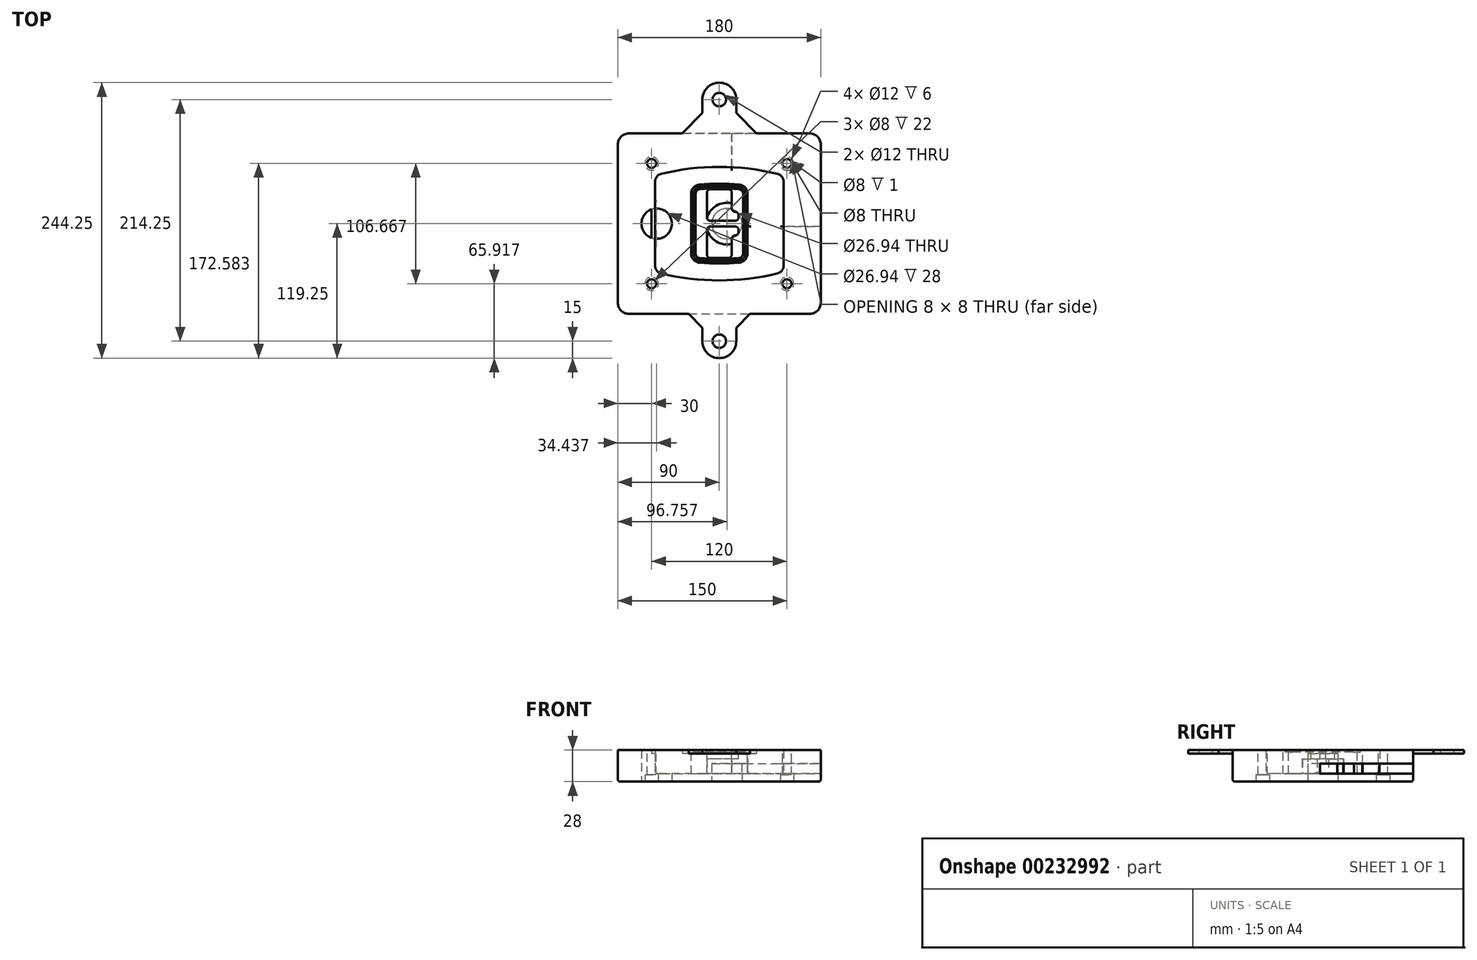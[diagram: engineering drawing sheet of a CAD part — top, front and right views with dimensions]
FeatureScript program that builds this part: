
annotation { "Feature Type Name" : "Feature", "Feature Type Description" : "" }
export const myFeature = defineFeature(function(context is Context, id is Id, definition is map)
    precondition{}
    {
        {
            var Q0;
            Q0=qCreatedBy(makeId("Top.planeOp"),FACE);
            var sketch = newSketch(context, id + "F0", { "sketchPlane" : qUnion([Q0])});
            skPoint(sketch, "E0.rect.middle", {"position": v(0, 0) * mm});
            skLineSegment(sketch, "E1.bottom", {"start": v(-80, -80) * mm, "end": v(80, -80) * mm});
            skLineSegment(sketch, "E1.top", {"start": v(-80, 80) * mm, "end": v(80, 80) * mm});
            skLineSegment(sketch, "E1.left", {"start": v(-90, -70) * mm, "end": v(-90, 70) * mm});
            skLineSegment(sketch, "E1.right", {"start": v(90, -70) * mm, "end": v(90, 70) * mm});
            skLineSegment(sketch, "E2", {"start": v(-90, 80) * mm, "end": v(90, -80) * mm, "construction": true});
            skLineSegment(sketch, "E3", {"start": v(90, 80) * mm, "end": v(-90, -80) * mm, "construction": true});
            skCircle(sketch, "E4", {"center": v(-60, 53.33) * mm, "radius": 4 * mm});
            skCircle(sketch, "E5", {"center": v(60, 53.33) * mm, "radius": 4 * mm});
            skCircle(sketch, "E6", {"center": v(60, -53.33) * mm, "radius": 4 * mm});
            skCircle(sketch, "E7", {"center": v(-60, -53.33) * mm, "radius": 4 * mm});
            skLineSegment(sketch, "E8", {"start": v(-60, 53.33) * mm, "end": v(60, 53.33) * mm, "construction": true});
            skLineSegment(sketch, "E9", {"start": v(60, 53.33) * mm, "end": v(60, -53.33) * mm, "construction": true});
            skLineSegment(sketch, "E10", {"start": v(60, -53.33) * mm, "end": v(-60, -53.33) * mm, "construction": true});
            skLineSegment(sketch, "E11", {"start": v(-60, -53.33) * mm, "end": v(-60, 53.33) * mm, "construction": true});
            skLineSegment(sketch, "E12", {"start": v(-60, 37.3) * mm, "end": v(-60, -37.3) * mm});
            skLineSegment(sketch, "E13", {"start": v(60, 37.3) * mm, "end": v(60, -37.3) * mm});
            skArc(sketch, "E14", {"start": v(52.38, 47.01) * mm, "mid": v(0, 53.33) * mm, "end": v(-52.38, 47.01) * mm});
            skArc(sketch, "E15", {"start": v(-52.38, -47.01) * mm, "mid": v(0, -53.33) * mm, "end": v(52.38, -47.01) * mm});
            skLineSegment(sketch, "E16", {"start": v(-60, 0) * mm, "end": v(60, 0) * mm, "construction": true});
            skPoint(sketch, "E17.visualSharp", {"position": v(-60, -45) * mm});
            skArc(sketch, "E17.filletArc", {"start": v(-60, -37.3) * mm, "mid": v(-57.87, -43.47) * mm, "end": v(-52.38, -47.01) * mm});
            skPoint(sketch, "E18.visualSharp", {"position": v(-60, 45) * mm});
            skArc(sketch, "E18.filletArc", {"start": v(-52.38, 47.01) * mm, "mid": v(-57.87, 43.47) * mm, "end": v(-60, 37.3) * mm});
            skPoint(sketch, "E19.visualSharp", {"position": v(60, 45) * mm});
            skArc(sketch, "E19.filletArc", {"start": v(60, 37.3) * mm, "mid": v(57.87, 43.47) * mm, "end": v(52.38, 47.01) * mm});
            skPoint(sketch, "E20.visualSharp", {"position": v(60, -45) * mm});
            skArc(sketch, "E20.filletArc", {"start": v(52.38, -47.01) * mm, "mid": v(57.87, -43.47) * mm, "end": v(60, -37.3) * mm});
            skPoint(sketch, "E21.visualSharp", {"position": v(-90, 80) * mm});
            skArc(sketch, "E21.filletArc", {"start": v(-80, 80) * mm, "mid": v(-87.07, 77.07) * mm, "end": v(-90, 70) * mm});
            skPoint(sketch, "E22.visualSharp", {"position": v(90, 80) * mm});
            skArc(sketch, "E22.filletArc", {"start": v(90, 70) * mm, "mid": v(87.07, 77.07) * mm, "end": v(80, 80) * mm});
            skPoint(sketch, "E23.visualSharp", {"position": v(90, -80) * mm});
            skArc(sketch, "E23.filletArc", {"start": v(80, -80) * mm, "mid": v(87.07, -77.07) * mm, "end": v(90, -70) * mm});
            skPoint(sketch, "E24.visualSharp", {"position": v(-90, -80) * mm});
            skArc(sketch, "E24.filletArc", {"start": v(-90, -70) * mm, "mid": v(-87.07, -77.07) * mm, "end": v(-80, -80) * mm});
            skArc(sketch, "E25.0", {"start": v(57, 37.3) * mm, "mid": v(55.5, 41.62) * mm, "end": v(51.67, 44.1) * mm});
            skLineSegment(sketch, "E25.1", {"start": v(57, 37.3) * mm, "end": v(57, -37.3) * mm});
            skArc(sketch, "E25.2", {"start": v(51.67, -44.1) * mm, "mid": v(55.5, -41.62) * mm, "end": v(57, -37.3) * mm});
            skArc(sketch, "E25.3", {"start": v(-51.67, -44.1) * mm, "mid": v(0, -50.33) * mm, "end": v(51.67, -44.1) * mm});
            skArc(sketch, "E25.4", {"start": v(-57, -37.3) * mm, "mid": v(-55.5, -41.62) * mm, "end": v(-51.67, -44.1) * mm});
            skArc(sketch, "E25.5", {"start": v(51.67, 44.1) * mm, "mid": v(0, 50.33) * mm, "end": v(-51.67, 44.1) * mm});
            skLineSegment(sketch, "E25.6", {"start": v(-57, 37.3) * mm, "end": v(-57, -37.3) * mm});
            skArc(sketch, "E25.7", {"start": v(-51.67, 44.1) * mm, "mid": v(-55.5, 41.62) * mm, "end": v(-57, 37.3) * mm});
            skArc(sketch, "E26.0", {"start": v(-53.33, 50.9) * mm, "mid": v(-61.01, 45.94) * mm, "end": v(-64, 37.3) * mm});
            skArc(sketch, "E26.1", {"start": v(53.33, 50.9) * mm, "mid": v(0, 57.33) * mm, "end": v(-53.33, 50.9) * mm});
            skArc(sketch, "E26.2", {"start": v(64, 37.3) * mm, "mid": v(61.01, 45.94) * mm, "end": v(53.33, 50.9) * mm});
            skLineSegment(sketch, "E26.3", {"start": v(64, 37.3) * mm, "end": v(64, -37.3) * mm});
            skArc(sketch, "E26.4", {"start": v(53.33, -50.9) * mm, "mid": v(61.01, -45.94) * mm, "end": v(64, -37.3) * mm});
            skLineSegment(sketch, "E26.5", {"start": v(-64, 37.3) * mm, "end": v(-64, -37.3) * mm});
            skArc(sketch, "E26.6", {"start": v(-53.33, -50.9) * mm, "mid": v(0, -57.33) * mm, "end": v(53.33, -50.9) * mm});
            skArc(sketch, "E26.7", {"start": v(-64, -37.3) * mm, "mid": v(-61.01, -45.94) * mm, "end": v(-53.33, -50.9) * mm});
            skSolve(sketch);
        }
        {
            var Q0;
            Q0=makeQuery(id+"F0.imprint","IMPRINT",FACE,{"disambiguationData":[TD([[makeQuery(id+"F0.imprint","IMPRINT",EDGE,{"derivedFrom":sQuery(id+"F0.wireOp",EDGE,"E1.bottom")}),1.0]])]});
            var Q1;
            Q1=makeQuery(id+"F0.imprint","IMPRINT",FACE,{"disambiguationData":[TD([[makeQuery(id+"F0.imprint","IMPRINT",EDGE,{"derivedFrom":sQuery(id+"F0.wireOp",EDGE,"E12")}),1.0]])]});
            var Q2;
            Q2=makeQuery(id+"F0.imprint","IMPRINT",FACE,{"disambiguationData":[TD([[makeQuery(id+"F0.imprint","IMPRINT",EDGE,{"derivedFrom":sQuery(id+"F0.wireOp",EDGE,"E25.0")}),1.0]])]});
            var Q3;
            Q3=makeQuery(id+"F0.imprint","IMPRINT",FACE,{"disambiguationData":[TD([[makeQuery(id+"F0.imprint","IMPRINT",EDGE,{"derivedFrom":sQuery(id+"F0.wireOp",EDGE,"E12")}),-1.0]])]});
            extrude(context, id + "F1", {"entities" : qUnion([Q0, Q1, Q2, Q3]), "oppositeDirection" : true, "depth" : 25 * mm});
        }
        {
            var Q0;
            Q0=makeQuery(id+"F0.imprint","IMPRINT",FACE,{"disambiguationData":[TD([[makeQuery(id+"F0.imprint","IMPRINT",EDGE,{"derivedFrom":sQuery(id+"F0.wireOp",EDGE,"E12")}),1.0]])]});
            extrude(context, id + "F2", {"entities" : qUnion([Q0]), "operationType" : NewBodyOperationType.ADD, "depth" : 3 * mm});
        }
        {
            var Q0;
            Q0=makeQuery(id+"F0.imprint","IMPRINT",FACE,{"disambiguationData":[TD([[makeQuery(id+"F0.imprint","IMPRINT",EDGE,{"derivedFrom":sQuery(id+"F0.wireOp",EDGE,"E25.0")}),1.0]])]});
            extrude(context, id + "F3", {"entities" : qUnion([Q0]), "operationType" : NewBodyOperationType.REMOVE, "oppositeDirection" : true, "depth" : 18 * mm});
        }
        {
            var Q0;
            Q0=makeQuery(id+"F2.opExtrude","CAP_FACE",FACE,{"disambiguationData":[OSD([sQuery(id+"F0.wireOp",EDGE,"E12"),sQuery(id+"F0.wireOp",EDGE,"E13"),sQuery(id+"F0.wireOp",EDGE,"E14"),sQuery(id+"F0.wireOp",EDGE,"E15"),sQuery(id+"F0.wireOp",EDGE,"E17.filletArc"),sQuery(id+"F0.wireOp",EDGE,"E18.filletArc"),sQuery(id+"F0.wireOp",EDGE,"E19.filletArc"),sQuery(id+"F0.wireOp",EDGE,"E20.filletArc"),sQuery(id+"F0.wireOp",EDGE,"E25.0"),sQuery(id+"F0.wireOp",EDGE,"E25.1"),sQuery(id+"F0.wireOp",EDGE,"E25.2"),sQuery(id+"F0.wireOp",EDGE,"E25.3"),sQuery(id+"F0.wireOp",EDGE,"E25.4"),sQuery(id+"F0.wireOp",EDGE,"E25.5"),sQuery(id+"F0.wireOp",EDGE,"E25.6"),sQuery(id+"F0.wireOp",EDGE,"E25.7")])],"isStart":false});
            var sketch = newSketch(context, id + "F4", { "sketchPlane" : qUnion([Q0])});
            skArc(sketch, "E27.0", {"start": v(-17.7, -34.56) * mm, "mid": v(0, -35.33) * mm, "end": v(17.7, -34.56) * mm});
            skArc(sketch, "E28.0", {"start": v(17.7, 34.56) * mm, "mid": v(0, 35.33) * mm, "end": v(-17.7, 34.56) * mm});
            skLineSegment(sketch, "E29", {"start": v(-25, 26.59) * mm, "end": v(-25, -26.59) * mm});
            skLineSegment(sketch, "E30", {"start": v(25, 26.59) * mm, "end": v(25, -26.59) * mm});
            skLineSegment(sketch, "E31", {"start": v(-25, 33.78) * mm, "end": v(25, 33.78) * mm, "construction": true});
            skLineSegment(sketch, "E32", {"start": v(-25, -33.78) * mm, "end": v(25, -33.78) * mm, "construction": true});
            skPoint(sketch, "E33.visualSharp", {"position": v(-25, 33.78) * mm});
            skArc(sketch, "E33.filletArc", {"start": v(-17.7, 34.56) * mm, "mid": v(-22.9, 32) * mm, "end": v(-25, 26.59) * mm});
            skPoint(sketch, "E34.visualSharp", {"position": v(25, 33.78) * mm});
            skArc(sketch, "E34.filletArc", {"start": v(25, 26.59) * mm, "mid": v(22.9, 32) * mm, "end": v(17.7, 34.56) * mm});
            skPoint(sketch, "E35.visualSharp", {"position": v(25, -33.78) * mm});
            skArc(sketch, "E35.filletArc", {"start": v(17.7, -34.56) * mm, "mid": v(22.9, -32) * mm, "end": v(25, -26.59) * mm});
            skPoint(sketch, "E36.visualSharp", {"position": v(-25, -33.78) * mm});
            skArc(sketch, "E36.filletArc", {"start": v(-25, -26.59) * mm, "mid": v(-22.9, -32) * mm, "end": v(-17.7, -34.56) * mm});
            skArc(sketch, "E37.0", {"start": v(51.67, 44.1) * mm, "mid": v(0, 50.33) * mm, "end": v(-51.67, 44.1) * mm});
            skArc(sketch, "E37.1", {"start": v(-51.67, 44.1) * mm, "mid": v(-55.5, 41.62) * mm, "end": v(-57, 37.3) * mm});
            skLineSegment(sketch, "E37.2", {"start": v(-57, 37.3) * mm, "end": v(-57, -37.3) * mm});
            skArc(sketch, "E37.3", {"start": v(-57, -37.3) * mm, "mid": v(-55.5, -41.62) * mm, "end": v(-51.67, -44.1) * mm});
            skArc(sketch, "E37.4", {"start": v(-51.67, -44.1) * mm, "mid": v(0, -50.33) * mm, "end": v(51.67, -44.1) * mm});
            skArc(sketch, "E37.5", {"start": v(51.67, -44.1) * mm, "mid": v(55.5, -41.62) * mm, "end": v(57, -37.3) * mm});
            skLineSegment(sketch, "E37.6", {"start": v(57, 37.3) * mm, "end": v(57, -37.3) * mm});
            skArc(sketch, "E37.7", {"start": v(57, 37.3) * mm, "mid": v(55.5, 41.62) * mm, "end": v(51.67, 44.1) * mm});
            skLineSegment(sketch, "E38.0", {"start": v(23, 26.59) * mm, "end": v(23, -26.59) * mm});
            skArc(sketch, "E38.1", {"start": v(17.53, -32.56) * mm, "mid": v(21.42, -30.64) * mm, "end": v(23, -26.59) * mm});
            skArc(sketch, "E38.2", {"start": v(-17.53, -32.56) * mm, "mid": v(0, -33.33) * mm, "end": v(17.53, -32.56) * mm});
            skArc(sketch, "E38.3", {"start": v(-23, -26.59) * mm, "mid": v(-21.42, -30.64) * mm, "end": v(-17.53, -32.56) * mm});
            skLineSegment(sketch, "E38.4", {"start": v(-23, 26.59) * mm, "end": v(-23, -26.59) * mm});
            skArc(sketch, "E38.5", {"start": v(23, 26.59) * mm, "mid": v(21.42, 30.64) * mm, "end": v(17.53, 32.56) * mm});
            skArc(sketch, "E38.6", {"start": v(-17.53, 32.56) * mm, "mid": v(-21.42, 30.64) * mm, "end": v(-23, 26.59) * mm});
            skArc(sketch, "E38.7", {"start": v(17.53, 32.56) * mm, "mid": v(0, 33.33) * mm, "end": v(-17.53, 32.56) * mm});
            skArc(sketch, "E39.0", {"start": v(21, 26.59) * mm, "mid": v(19.95, 29.29) * mm, "end": v(17.35, 30.57) * mm});
            skLineSegment(sketch, "E39.1", {"start": v(21, 26.59) * mm, "end": v(21, -26.59) * mm});
            skArc(sketch, "E39.2", {"start": v(17.35, -30.57) * mm, "mid": v(19.95, -29.29) * mm, "end": v(21, -26.59) * mm});
            skArc(sketch, "E39.3", {"start": v(-17.35, -30.57) * mm, "mid": v(0, -31.33) * mm, "end": v(17.35, -30.57) * mm});
            skArc(sketch, "E39.4", {"start": v(-21, -26.59) * mm, "mid": v(-19.95, -29.29) * mm, "end": v(-17.35, -30.57) * mm});
            skArc(sketch, "E39.5", {"start": v(17.35, 30.57) * mm, "mid": v(0, 31.33) * mm, "end": v(-17.35, 30.57) * mm});
            skLineSegment(sketch, "E39.6", {"start": v(-21, 26.59) * mm, "end": v(-21, -26.59) * mm});
            skArc(sketch, "E39.7", {"start": v(-17.35, 30.57) * mm, "mid": v(-19.95, 29.29) * mm, "end": v(-21, 26.59) * mm});
            skLineSegment(sketch, "E40", {"start": v(-25, 0) * mm, "end": v(25, 0) * mm, "construction": true});
            skLineSegment(sketch, "E41", {"start": v(-11, 5.5) * mm, "end": v(-11, 27.5) * mm});
            skLineSegment(sketch, "E42", {"start": v(-8, 30.5) * mm, "end": v(8, 30.5) * mm});
            skLineSegment(sketch, "E43", {"start": v(11, 27.5) * mm, "end": v(11, 13.5) * mm});
            skLineSegment(sketch, "E44", {"start": v(14, 10.5) * mm, "end": v(14, 10.5) * mm});
            skLineSegment(sketch, "E45", {"start": v(17, 7.5) * mm, "end": v(17, 5.5) * mm});
            skLineSegment(sketch, "E46", {"start": v(14, 2.5) * mm, "end": v(-8, 2.5) * mm});
            skPoint(sketch, "E47.visualSharp", {"position": v(-11, 30.5) * mm});
            skArc(sketch, "E47.filletArc", {"start": v(-8, 30.5) * mm, "mid": v(-10.12, 29.62) * mm, "end": v(-11, 27.5) * mm});
            skPoint(sketch, "E48.visualSharp", {"position": v(11, 30.5) * mm});
            skArc(sketch, "E48.filletArc", {"start": v(11, 27.5) * mm, "mid": v(10.12, 29.62) * mm, "end": v(8, 30.5) * mm});
            skPoint(sketch, "E49.visualSharp", {"position": v(11, 10.5) * mm});
            skArc(sketch, "E49.filletArc", {"start": v(11, 13.5) * mm, "mid": v(11.88, 11.38) * mm, "end": v(14, 10.5) * mm});
            skPoint(sketch, "E50.visualSharp", {"position": v(17, 10.5) * mm});
            skArc(sketch, "E50.filletArc", {"start": v(17, 7.5) * mm, "mid": v(16.12, 9.62) * mm, "end": v(14, 10.5) * mm});
            skPoint(sketch, "E51.visualSharp", {"position": v(17, 2.5) * mm});
            skArc(sketch, "E51.filletArc", {"start": v(14, 2.5) * mm, "mid": v(16.12, 3.38) * mm, "end": v(17, 5.5) * mm});
            skPoint(sketch, "E52.visualSharp", {"position": v(-11, 2.5) * mm});
            skArc(sketch, "E52.filletArc", {"start": v(-11, 5.5) * mm, "mid": v(-10.12, 3.38) * mm, "end": v(-8, 2.5) * mm});
            skLineSegment(sketch, "E53.0.MirrorCS", {"start": v(14, -2.5) * mm, "end": v(-8, -2.5) * mm});
            skArc(sketch, "E54.0.MirrorCS", {"start": v(-11, -5.5) * mm, "mid": v(-10.12, -3.38) * mm, "end": v(-8, -2.5) * mm});
            skLineSegment(sketch, "E55.0.MirrorCS", {"start": v(-11, -5.5) * mm, "end": v(-11, -27.5) * mm});
            skArc(sketch, "E56.0.MirrorCS", {"start": v(-8, -30.5) * mm, "mid": v(-10.12, -29.62) * mm, "end": v(-11, -27.5) * mm});
            skLineSegment(sketch, "E57.0.MirrorCS", {"start": v(-8, -30.5) * mm, "end": v(8, -30.5) * mm});
            skArc(sketch, "E58.0.MirrorCS", {"start": v(11, -27.5) * mm, "mid": v(10.12, -29.62) * mm, "end": v(8, -30.5) * mm});
            skLineSegment(sketch, "E59.0.MirrorCS", {"start": v(11, -27.5) * mm, "end": v(11, -13.5) * mm});
            skArc(sketch, "E60.0.MirrorCS", {"start": v(11, -13.5) * mm, "mid": v(11.88, -11.38) * mm, "end": v(14, -10.5) * mm});
            skArc(sketch, "E61.0.MirrorCS", {"start": v(17, -7.5) * mm, "mid": v(16.12, -9.62) * mm, "end": v(14, -10.5) * mm});
            skLineSegment(sketch, "E62.0.MirrorCS", {"start": v(17, -7.5) * mm, "end": v(17, -5.5) * mm});
            skArc(sketch, "E63.0.MirrorCS", {"start": v(14, -2.5) * mm, "mid": v(16.12, -3.38) * mm, "end": v(17, -5.5) * mm});
            skSolve(sketch);
        }
        {
            var Q0;
            Q0=makeQuery(id+"F4.imprint","IMPRINT",FACE,{"disambiguationData":[TD([[makeQuery(id+"F4.imprint","IMPRINT",EDGE,{"derivedFrom":sQuery(id+"F4.wireOp",EDGE,"E27.0")}),1.0]])]});
            var Q1;
            Q1=makeQuery(id+"F4.imprint","IMPRINT",FACE,{"disambiguationData":[TD([[makeQuery(id+"F4.imprint","IMPRINT",EDGE,{"derivedFrom":sQuery(id+"F4.wireOp",EDGE,"E38.0")}),-1.0]])]});
            var Q2;
            Q2=makeQuery(id+"F4.imprint","IMPRINT",FACE,{"disambiguationData":[TD([[makeQuery(id+"F4.imprint","IMPRINT",EDGE,{"derivedFrom":sQuery(id+"F4.wireOp",EDGE,"E39.0")}),1.0]])]});
            extrude(context, id + "F5", {"entities" : qUnion([Q0, Q1, Q2]), "operationType" : NewBodyOperationType.ADD, "endBound" : BoundingType.UP_TO_NEXT, "oppositeDirection" : true, "depth" : 25 * mm});
        }
        {
            var Q0;
            Q0=makeQuery(id+"F4.imprint","IMPRINT",FACE,{"disambiguationData":[TD([[makeQuery(id+"F4.imprint","IMPRINT",EDGE,{"derivedFrom":sQuery(id+"F4.wireOp",EDGE,"E38.0")}),-1.0]])]});
            extrude(context, id + "F6", {"entities" : qUnion([Q0]), "operationType" : NewBodyOperationType.REMOVE, "oppositeDirection" : true, "depth" : 2 * mm});
        }
        {
            var Q0;
            Q0=makeQuery(id+"F1.opExtrude","CAP_FACE",FACE,{"disambiguationData":[OSD([sQuery(id+"F0.wireOp",EDGE,"E1.bottom"),sQuery(id+"F0.wireOp",EDGE,"E1.top"),sQuery(id+"F0.wireOp",EDGE,"E1.left"),sQuery(id+"F0.wireOp",EDGE,"E1.right"),sQuery(id+"F0.wireOp",EDGE,"E4"),sQuery(id+"F0.wireOp",EDGE,"E5"),sQuery(id+"F0.wireOp",EDGE,"E6"),sQuery(id+"F0.wireOp",EDGE,"E7"),sQuery(id+"F0.wireOp",EDGE,"E21.filletArc"),sQuery(id+"F0.wireOp",EDGE,"E22.filletArc"),sQuery(id+"F0.wireOp",EDGE,"E23.filletArc"),sQuery(id+"F0.wireOp",EDGE,"E24.filletArc")])],"isStart":false});
            var sketch = newSketch(context, id + "F7", { "sketchPlane" : qUnion([Q0])});
            skCircle(sketch, "E64", {"center": v(6.76, 0) * mm, "radius": 13.47 * mm});
            skCircle(sketch, "E65", {"center": v(-55.56, 0) * mm, "radius": 13.47 * mm});
            skLineSegment(sketch, "E66", {"start": v(90, 0) * mm, "end": v(-90, 0) * mm});
            skCircle(sketch, "E67", {"center": v(6.76, 0) * mm, "radius": 18.47 * mm});
            skCircle(sketch, "E68", {"center": v(60, -53.33) * mm, "radius": 6 * mm});
            skCircle(sketch, "E69", {"center": v(-60, -53.33) * mm, "radius": 6 * mm});
            skCircle(sketch, "E70", {"center": v(-60, 53.33) * mm, "radius": 6 * mm});
            skCircle(sketch, "E71", {"center": v(60, 53.33) * mm, "radius": 6 * mm});
            skSolve(sketch);
        }
        {
            var Q0;
            {var subQ1=sQuery(id+"F7.wireOp",EDGE,"E66");var subQ4=sQuery(id+"F7.wireOp",EDGE,"E64");var subQ6=makeQuery(id+"F7.imprint","INTERSECT",VERTEX,{"disambiguationData":[OD(0.0)],"derivedFrom":[subQ4,subQ1]});Q0=makeQuery(id+"F7.imprint","IMPRINT",FACE,{"disambiguationData":[TD([[makeQuery(id+"F7.imprint","IMPRINT",EDGE,{"disambiguationData":[TD([[subQ6,-1.0]])],"derivedFrom":subQ4}),-1.0]])]});}
            var Q1;
            {var subQ0=sQuery(id+"F7.wireOp",EDGE,"E66");var subQ1=sQuery(id+"F7.wireOp",EDGE,"E64");var subQ3=makeQuery(id+"F7.imprint","INTERSECT",VERTEX,{"disambiguationData":[OD(0.0)],"derivedFrom":[subQ1,subQ0]});Q1=makeQuery(id+"F7.imprint","IMPRINT",FACE,{"disambiguationData":[TD([[makeQuery(id+"F7.imprint","IMPRINT",EDGE,{"disambiguationData":[TD([[subQ3,-1.0]])],"derivedFrom":subQ1}),1.0]])]});}
            var Q2;
            {var subQ0=sQuery(id+"F7.wireOp",EDGE,"E66");var subQ1=sQuery(id+"F7.wireOp",EDGE,"E64");var subQ3=makeQuery(id+"F7.imprint","INTERSECT",VERTEX,{"disambiguationData":[OD(0.0)],"derivedFrom":[subQ1,subQ0]});Q2=makeQuery(id+"F7.imprint","IMPRINT",FACE,{"disambiguationData":[TD([[makeQuery(id+"F7.imprint","IMPRINT",EDGE,{"disambiguationData":[TD([[subQ3,1.0]])],"derivedFrom":subQ1}),1.0]])]});}
            var Q3;
            {var subQ1=sQuery(id+"F7.wireOp",EDGE,"E66");var subQ4=sQuery(id+"F7.wireOp",EDGE,"E64");var subQ6=makeQuery(id+"F7.imprint","INTERSECT",VERTEX,{"disambiguationData":[OD(0.0)],"derivedFrom":[subQ4,subQ1]});Q3=makeQuery(id+"F7.imprint","IMPRINT",FACE,{"disambiguationData":[TD([[makeQuery(id+"F7.imprint","IMPRINT",EDGE,{"disambiguationData":[TD([[subQ6,1.0]])],"derivedFrom":subQ4}),-1.0]])]});}
            extrude(context, id + "F8", {"entities" : qUnion([Q0, Q1, Q2, Q3]), "operationType" : NewBodyOperationType.ADD, "oppositeDirection" : true, "depth" : 20 * mm});
        }
        {
            var Q0;
            {var subQ0=sQuery(id+"F7.wireOp",EDGE,"E66");var subQ1=sQuery(id+"F7.wireOp",EDGE,"E64");var subQ3=makeQuery(id+"F7.imprint","INTERSECT",VERTEX,{"disambiguationData":[OD(0.0)],"derivedFrom":[subQ1,subQ0]});Q0=makeQuery(id+"F7.imprint","IMPRINT",FACE,{"disambiguationData":[TD([[makeQuery(id+"F7.imprint","IMPRINT",EDGE,{"disambiguationData":[TD([[subQ3,-1.0]])],"derivedFrom":subQ1}),1.0]])]});}
            var Q1;
            {var subQ0=sQuery(id+"F7.wireOp",EDGE,"E66");var subQ1=sQuery(id+"F7.wireOp",EDGE,"E64");var subQ3=makeQuery(id+"F7.imprint","INTERSECT",VERTEX,{"disambiguationData":[OD(0.0)],"derivedFrom":[subQ1,subQ0]});Q1=makeQuery(id+"F7.imprint","IMPRINT",FACE,{"disambiguationData":[TD([[makeQuery(id+"F7.imprint","IMPRINT",EDGE,{"disambiguationData":[TD([[subQ3,1.0]])],"derivedFrom":subQ1}),1.0]])]});}
            extrude(context, id + "F9", {"entities" : qUnion([Q0, Q1]), "operationType" : NewBodyOperationType.REMOVE, "oppositeDirection" : true, "depth" : 16 * mm});
        }
        {
            var Q0;
            {var subQ0=sQuery(id+"F7.wireOp",EDGE,"E66");var subQ1=sQuery(id+"F7.wireOp",EDGE,"E65");var subQ3=makeQuery(id+"F7.imprint","INTERSECT",VERTEX,{"disambiguationData":[OD(0.0)],"derivedFrom":[subQ1,subQ0]});Q0=makeQuery(id+"F7.imprint","IMPRINT",FACE,{"disambiguationData":[TD([[makeQuery(id+"F7.imprint","IMPRINT",EDGE,{"disambiguationData":[TD([[subQ3,-1.0]])],"derivedFrom":subQ1}),1.0]])]});}
            var Q1;
            {var subQ0=sQuery(id+"F7.wireOp",EDGE,"E66");var subQ1=sQuery(id+"F7.wireOp",EDGE,"E65");var subQ3=makeQuery(id+"F7.imprint","INTERSECT",VERTEX,{"disambiguationData":[OD(0.0)],"derivedFrom":[subQ1,subQ0]});Q1=makeQuery(id+"F7.imprint","IMPRINT",FACE,{"disambiguationData":[TD([[makeQuery(id+"F7.imprint","IMPRINT",EDGE,{"disambiguationData":[TD([[subQ3,1.0]])],"derivedFrom":subQ1}),1.0]])]});}
            extrude(context, id + "F10", {"entities" : qUnion([Q0, Q1]), "operationType" : NewBodyOperationType.REMOVE, "oppositeDirection" : true, "depth" : 25 * mm});
        }
        {
            var Q0;
            Q0=makeQuery(id+"F7.imprint","IMPRINT",FACE,{"disambiguationData":[TD([[makeQuery(id+"F7.imprint","IMPRINT",EDGE,{"derivedFrom":sQuery(id+"F7.wireOp",EDGE,"E68")}),1.0]])]});
            var Q1;
            Q1=makeQuery(id+"F7.imprint","IMPRINT",FACE,{"disambiguationData":[TD([[makeQuery(id+"F7.imprint","IMPRINT",EDGE,{"derivedFrom":makeQuery(id+"F1.opExtrude","CAP_EDGE",EDGE,{"disambiguationData":[OSD([sQuery(id+"F0.wireOp",EDGE,"E5")])],"isStart":false})}),-1.0]])]});
            var Q2;
            Q2=makeQuery(id+"F7.imprint","IMPRINT",FACE,{"disambiguationData":[TD([[makeQuery(id+"F7.imprint","IMPRINT",EDGE,{"derivedFrom":sQuery(id+"F7.wireOp",EDGE,"E69")}),1.0]])]});
            var Q3;
            Q3=makeQuery(id+"F7.imprint","IMPRINT",FACE,{"disambiguationData":[TD([[makeQuery(id+"F7.imprint","IMPRINT",EDGE,{"derivedFrom":makeQuery(id+"F1.opExtrude","CAP_EDGE",EDGE,{"disambiguationData":[OSD([sQuery(id+"F0.wireOp",EDGE,"E4")])],"isStart":false})}),-1.0]])]});
            var Q4;
            Q4=makeQuery(id+"F7.imprint","IMPRINT",FACE,{"disambiguationData":[TD([[makeQuery(id+"F7.imprint","IMPRINT",EDGE,{"derivedFrom":sQuery(id+"F7.wireOp",EDGE,"E70")}),1.0]])]});
            var Q5;
            Q5=makeQuery(id+"F7.imprint","IMPRINT",FACE,{"disambiguationData":[TD([[makeQuery(id+"F7.imprint","IMPRINT",EDGE,{"derivedFrom":makeQuery(id+"F1.opExtrude","CAP_EDGE",EDGE,{"disambiguationData":[OSD([sQuery(id+"F0.wireOp",EDGE,"E7")])],"isStart":false})}),-1.0]])]});
            var Q6;
            Q6=makeQuery(id+"F7.imprint","IMPRINT",FACE,{"disambiguationData":[TD([[makeQuery(id+"F7.imprint","IMPRINT",EDGE,{"derivedFrom":sQuery(id+"F7.wireOp",EDGE,"E71")}),1.0]])]});
            var Q7;
            Q7=makeQuery(id+"F7.imprint","IMPRINT",FACE,{"disambiguationData":[TD([[makeQuery(id+"F7.imprint","IMPRINT",EDGE,{"derivedFrom":makeQuery(id+"F1.opExtrude","CAP_EDGE",EDGE,{"disambiguationData":[OSD([sQuery(id+"F0.wireOp",EDGE,"E6")])],"isStart":false})}),-1.0]])]});
            extrude(context, id + "F11", {"entities" : qUnion([Q0, Q1, Q2, Q3, Q4, Q5, Q6, Q7]), "operationType" : NewBodyOperationType.REMOVE, "oppositeDirection" : true, "depth" : 6 * mm});
        }
        {
            var Q0;
            Q0=makeQuery(id+"F9.boolean.opBoolean","COPY",FACE,{"derivedFrom":makeQuery(id+"F9.opExtrude","CAP_FACE",FACE,{"disambiguationData":[OSD([sQuery(id+"F7.wireOp",EDGE,"E64")])],"isStart":false})});
            var sketch = newSketch(context, id + "F12", { "sketchPlane" : qUnion([Q0])});
            skArc(sketch, "E72.0", {"start": v(11, -88.19) * mm, "mid": v(97.1, -83.6) * mm, "end": v(92.5, 2.5) * mm});
            skLineSegment(sketch, "E72.1", {"start": v(11, -17.97) * mm, "end": v(11, -17.97) * mm});
            skLineSegment(sketch, "E73", {"start": v(92.5, -105.13) * mm, "end": v(102.3, -105.13) * mm});
            skLineSegment(sketch, "E74.0", {"start": v(92.5, 2.5) * mm, "end": v(14, 2.5) * mm});
            skArc(sketch, "E74.1", {"start": v(14, 2.5) * mm, "mid": v(16.12, 3.38) * mm, "end": v(17, 5.5) * mm});
            skLineSegment(sketch, "E74.2", {"start": v(17, 7.5) * mm, "end": v(17, 5.5) * mm});
            skArc(sketch, "E74.3", {"start": v(17, 7.5) * mm, "mid": v(16.12, 9.62) * mm, "end": v(14, 10.5) * mm});
            skArc(sketch, "E74.4", {"start": v(11, 13.5) * mm, "mid": v(11.88, 11.38) * mm, "end": v(14, 10.5) * mm});
            skLineSegment(sketch, "E74.5", {"start": v(11, 13.5) * mm, "end": v(11, -88.19) * mm});
            skLineSegment(sketch, "E74.7", {"start": v(92.5, -2.5) * mm, "end": v(14, -2.5) * mm});
            skArc(sketch, "E74.8", {"start": v(14, -2.5) * mm, "mid": v(16.12, -3.38) * mm, "end": v(17, -5.5) * mm});
            skLineSegment(sketch, "E74.9", {"start": v(17, -7.5) * mm, "end": v(17, -5.5) * mm});
            skArc(sketch, "E74.10", {"start": v(17, -7.5) * mm, "mid": v(16.12, -9.62) * mm, "end": v(14, -10.5) * mm});
            skArc(sketch, "E74.11", {"start": v(11, -13.5) * mm, "mid": v(11.88, -11.38) * mm, "end": v(14, -10.5) * mm});
            skLineSegment(sketch, "E74.12", {"start": v(11, -17.97) * mm, "end": v(11, -13.5) * mm});
            skPoint(sketch, "E75.orphan", {"position": v(11, -27.5) * mm});
            skPoint(sketch, "E76.orphan", {"position": v(-8, -2.5) * mm});
            skPoint(sketch, "E77.orphan", {"position": v(-8, 2.5) * mm});
            skPoint(sketch, "E78.orphan", {"position": v(11, 27.5) * mm});
            skSolve(sketch);
        }
        {
            var Q0;
            {var subQ7=sQuery(id+"F12.wireOp",EDGE,"E72.0");var subQ14=sQuery(id+"F12.wireOp",EDGE,"E72.1");var subQ16=sQuery(id+"F12.wireOp",EDGE,"E74.1");var subQ18=sQuery(id+"F12.wireOp",EDGE,"E74.8");Q0=qUnion([makeQuery(id+"F12.imprint","IMPRINT",FACE,{"disambiguationData":[TD([[makeQuery(id+"F12.imprint","IMPRINT",EDGE,{"derivedFrom":subQ7}),1.0]])]}),makeQuery(id+"F12.imprint","IMPRINT",FACE,{"disambiguationData":[TD([[makeQuery(id+"F12.imprint","IMPRINT",EDGE,{"derivedFrom":subQ14}),1.0]])]}),makeQuery(id+"F12.imprint","IMPRINT",FACE,{"disambiguationData":[TD([[makeQuery(id+"F12.imprint","IMPRINT",EDGE,{"derivedFrom":subQ16}),1.0]])]}),makeQuery(id+"F12.imprint","IMPRINT",FACE,{"disambiguationData":[TD([[makeQuery(id+"F12.imprint","IMPRINT",EDGE,{"derivedFrom":subQ18}),-1.0]])]})]);}
            var Q1;
            Q1=makeQuery(id+"F5.boolean.opBoolean","SPLIT",FACE,{"disambiguationData":[TD([makeQuery(id+"F5.opExtrude","SWEPT_FACE",FACE,{"disambiguationData":[OSD([sQuery(id+"F4.wireOp",EDGE,"E41")])]})])],"derivedFrom":makeQuery(id+"F3.boolean.opBoolean","COPY",FACE,{"derivedFrom":makeQuery(id+"F3.opExtrude","CAP_FACE",FACE,{"disambiguationData":[OSD([sQuery(id+"F0.wireOp",EDGE,"E25.0"),sQuery(id+"F0.wireOp",EDGE,"E25.1"),sQuery(id+"F0.wireOp",EDGE,"E25.2"),sQuery(id+"F0.wireOp",EDGE,"E25.3"),sQuery(id+"F0.wireOp",EDGE,"E25.4"),sQuery(id+"F0.wireOp",EDGE,"E25.5"),sQuery(id+"F0.wireOp",EDGE,"E25.6"),sQuery(id+"F0.wireOp",EDGE,"E25.7")])],"isStart":false})})});
            extrude(context, id + "F13", {"entities" : qUnion([Q0]), "operationType" : NewBodyOperationType.REMOVE, "endBound" : BoundingType.UP_TO_SURFACE, "endBoundEntityFace" : qUnion([Q1]), "depth" : 25 * mm});
        }
        {
            var Q0;
            Q0=makeQuery(id+"F3.boolean.opBoolean","COPY",EDGE,{"derivedFrom":makeQuery(id+"F3.opExtrude","CAP_EDGE",EDGE,{"disambiguationData":[OSD([sQuery(id+"F0.wireOp",EDGE,"E25.6")])],"isStart":false})});
            var Q1;
            Q1=makeQuery(id+"F8.boolean.opBoolean","INTERSECT",EDGE,{"derivedFrom":[makeQuery(id+"F5.opExtrude","SWEPT_FACE",FACE,{"disambiguationData":[OSD([sQuery(id+"F4.wireOp",EDGE,"E30")])]}),makeQuery(id+"F8.opExtrude","CAP_FACE",FACE,{"disambiguationData":[OSD([sQuery(id+"F7.wireOp",EDGE,"E67")])],"isStart":false})]});
            var Q2;
            Q2=makeQuery(id+"F8.boolean.opBoolean","INTERSECT",EDGE,{"disambiguationData":[OD(1.0)],"derivedFrom":[makeQuery(id+"F5.opExtrude","SWEPT_FACE",FACE,{"disambiguationData":[OSD([sQuery(id+"F4.wireOp",EDGE,"E30")])]}),makeQuery(id+"F8.opExtrude","SWEPT_FACE",FACE,{"disambiguationData":[OSD([sQuery(id+"F7.wireOp",EDGE,"E67")])]})]});
            var Q3;
            {var subQ0=makeQuery(id+"F3.boolean.opBoolean","COPY",FACE,{"derivedFrom":makeQuery(id+"F3.opExtrude","CAP_FACE",FACE,{"disambiguationData":[OSD([sQuery(id+"F0.wireOp",EDGE,"E25.0"),sQuery(id+"F0.wireOp",EDGE,"E25.1"),sQuery(id+"F0.wireOp",EDGE,"E25.2"),sQuery(id+"F0.wireOp",EDGE,"E25.3"),sQuery(id+"F0.wireOp",EDGE,"E25.4"),sQuery(id+"F0.wireOp",EDGE,"E25.5"),sQuery(id+"F0.wireOp",EDGE,"E25.6"),sQuery(id+"F0.wireOp",EDGE,"E25.7")])],"isStart":false})});var subQ1=sQuery(id+"F4.wireOp",EDGE,"E30");Q3=makeQuery(id+"F8.boolean.opBoolean","SPLIT",EDGE,{"disambiguationData":[TD([makeQuery(id+"F5.opExtrude","SWEPT_FACE",FACE,{"disambiguationData":[OSD([sQuery(id+"F4.wireOp",EDGE,"E35.filletArc")])]})])],"derivedFrom":makeQuery(id+"F5.opExtrude","TWEAK_EDGE",EDGE,{"derivedFrom":[subQ0,makeQuery(id+"F4.imprint","IMPRINT",EDGE,{"derivedFrom":subQ1})]})});}
            var Q4;
            {var subQ0=sQuery(id+"F0.wireOp",EDGE,"E25.0");var subQ1=sQuery(id+"F0.wireOp",EDGE,"E25.1");var subQ2=sQuery(id+"F0.wireOp",EDGE,"E25.2");var subQ3=sQuery(id+"F0.wireOp",EDGE,"E25.3");var subQ4=sQuery(id+"F0.wireOp",EDGE,"E25.4");var subQ5=sQuery(id+"F0.wireOp",EDGE,"E25.5");var subQ6=sQuery(id+"F0.wireOp",EDGE,"E25.6");var subQ7=sQuery(id+"F0.wireOp",EDGE,"E25.7");Q4=makeQuery(id+"F8.boolean.opBoolean","INTERSECT",EDGE,{"derivedFrom":[makeQuery(id+"F5.boolean.opBoolean","SPLIT",FACE,{"disambiguationData":[TD([makeQuery(id+"F2.opExtrude","SWEPT_FACE",FACE,{"disambiguationData":[OSD([subQ0])]})])],"derivedFrom":makeQuery(id+"F3.boolean.opBoolean","COPY",FACE,{"derivedFrom":makeQuery(id+"F3.opExtrude","CAP_FACE",FACE,{"disambiguationData":[OSD([subQ0,subQ1,subQ2,subQ3,subQ4,subQ5,subQ6,subQ7])],"isStart":false})})}),makeQuery(id+"F8.opExtrude","SWEPT_FACE",FACE,{"disambiguationData":[OSD([sQuery(id+"F7.wireOp",EDGE,"E67")])]})]});}
            var Q5;
            Q5=makeQuery(id+"F8.boolean.opBoolean","INTERSECT",EDGE,{"disambiguationData":[OD(0.0)],"derivedFrom":[makeQuery(id+"F5.opExtrude","SWEPT_FACE",FACE,{"disambiguationData":[OSD([sQuery(id+"F4.wireOp",EDGE,"E30")])]}),makeQuery(id+"F8.opExtrude","SWEPT_FACE",FACE,{"disambiguationData":[OSD([sQuery(id+"F7.wireOp",EDGE,"E67")])]})]});
            fillet(context, id + "F14", {"entities" : qUnion([Q0, Q1, Q2, Q3, Q4, Q5]), "radius" : 3 * mm, "tangentPropagation" : true, "allowEdgeOverflow" : false});
        }
        {
            var Q0;
            Q0=makeQuery(id+"F1.opExtrude","CAP_EDGE",EDGE,{"disambiguationData":[OSD([sQuery(id+"F0.wireOp",EDGE,"E1.bottom")])],"isStart":false});
            fillet(context, id + "F15", {"entities" : qUnion([Q0]), "radius" : 2 * mm, "tangentPropagation" : true, "allowEdgeOverflow" : false});
        }
        {
            var Q0;
            {var subQ0=sQuery(id+"F0.wireOp",EDGE,"E22.filletArc");var subQ1=sQuery(id+"F0.wireOp",EDGE,"E7");var subQ2=sQuery(id+"F0.wireOp",EDGE,"E6");var subQ3=sQuery(id+"F0.wireOp",EDGE,"E5");var subQ4=sQuery(id+"F0.wireOp",EDGE,"E4");var subQ5=sQuery(id+"F0.wireOp",EDGE,"E1.bottom");var subQ6=sQuery(id+"F0.wireOp",EDGE,"E21.filletArc");var subQ7=sQuery(id+"F0.wireOp",EDGE,"E1.top");var subQ8=sQuery(id+"F0.wireOp",EDGE,"E1.left");var subQ9=sQuery(id+"F0.wireOp",EDGE,"E1.right");var subQ10=sQuery(id+"F0.wireOp",EDGE,"E23.filletArc");var subQ11=sQuery(id+"F0.wireOp",EDGE,"E24.filletArc");Q0=makeQuery(id+"F2.boolean.opBoolean","SPLIT",FACE,{"disambiguationData":[TD([makeQuery(id+"F1.opExtrude","SWEPT_FACE",FACE,{"disambiguationData":[OSD([subQ5])]})])],"derivedFrom":makeQuery(id+"F1.opExtrude","CAP_FACE",FACE,{"disambiguationData":[OSD([subQ5,subQ7,subQ8,subQ9,subQ4,subQ3,subQ2,subQ1,subQ6,subQ0,subQ10,subQ11])],"isStart":true})});}
            var sketch = newSketch(context, id + "F16", { "sketchPlane" : qUnion([Q0])});
            skLineSegment(sketch, "E79.0", {"start": v(-80, 80) * mm, "end": v(80, 80) * mm});
            skArc(sketch, "E79.1", {"start": v(90, 70) * mm, "mid": v(87.07, 77.07) * mm, "end": v(80, 80) * mm});
            skLineSegment(sketch, "E79.2", {"start": v(90, -70) * mm, "end": v(90, 70) * mm});
            skArc(sketch, "E79.3", {"start": v(80, -80) * mm, "mid": v(87.07, -77.07) * mm, "end": v(90, -70) * mm});
            skLineSegment(sketch, "E79.4", {"start": v(-80, -80) * mm, "end": v(80, -80) * mm});
            skArc(sketch, "E79.5", {"start": v(-90, -70) * mm, "mid": v(-87.07, -77.07) * mm, "end": v(-80, -80) * mm});
            skLineSegment(sketch, "E79.6", {"start": v(-90, -70) * mm, "end": v(-90, 70) * mm});
            skPoint(sketch, "E79.7", {"position": v(-80, 80) * mm});
            skArc(sketch, "E79.8", {"start": v(52.38, 47.01) * mm, "mid": v(0, 53.33) * mm, "end": v(-52.38, 47.01) * mm});
            skLineSegment(sketch, "E79.9", {"start": v(-60, 37.3) * mm, "end": v(-60, -37.3) * mm});
            skArc(sketch, "E79.10", {"start": v(-52.38, 47.01) * mm, "mid": v(-57.87, 43.47) * mm, "end": v(-60, 37.3) * mm});
            skArc(sketch, "E79.11", {"start": v(-60, -37.3) * mm, "mid": v(-57.87, -43.47) * mm, "end": v(-52.38, -47.01) * mm});
            skArc(sketch, "E79.12", {"start": v(-52.38, -47.01) * mm, "mid": v(0, -53.33) * mm, "end": v(52.38, -47.01) * mm});
            skArc(sketch, "E79.13", {"start": v(52.38, -47.01) * mm, "mid": v(57.87, -43.47) * mm, "end": v(60, -37.3) * mm});
            skLineSegment(sketch, "E79.14", {"start": v(60, 37.3) * mm, "end": v(60, -37.3) * mm});
            skArc(sketch, "E79.15", {"start": v(60, 37.3) * mm, "mid": v(57.87, 43.47) * mm, "end": v(52.38, 47.01) * mm});
            skArc(sketch, "E79.16", {"start": v(-80, 80) * mm, "mid": v(-87.07, 77.07) * mm, "end": v(-90, 70) * mm});
            skPoint(sketch, "E79.17", {"position": v(57.87, -43.47) * mm});
            skCircle(sketch, "E80", {"center": v(0, 110) * mm, "radius": 6 * mm});
            skLineSegment(sketch, "E81", {"start": v(-15, 98) * mm, "end": v(-33, 80) * mm});
            skLineSegment(sketch, "E82", {"start": v(15, 98) * mm, "end": v(33, 80) * mm});
            skLineSegment(sketch, "E83", {"start": v(15, 98) * mm, "end": v(15, 110) * mm});
            skLineSegment(sketch, "E84", {"start": v(-15, 98) * mm, "end": v(-15, 110) * mm});
            skArc(sketch, "E85", {"start": v(15, 110) * mm, "mid": v(0, 125) * mm, "end": v(-15, 110) * mm});
            skLineSegment(sketch, "E86.MirrorCS", {"start": v(15, -92.25) * mm, "end": v(33, -74.25) * mm});
            skLineSegment(sketch, "E87.MirrorCS", {"start": v(15, -92.25) * mm, "end": v(15, -104.25) * mm});
            skArc(sketch, "E88.MirrorCS", {"start": v(15, -104.25) * mm, "mid": v(0, -119.25) * mm, "end": v(-15, -104.25) * mm});
            skLineSegment(sketch, "E89.MirrorCS", {"start": v(-15, -92.25) * mm, "end": v(-15, -104.25) * mm});
            skLineSegment(sketch, "E90.MirrorCS", {"start": v(-15, -92.25) * mm, "end": v(-33, -74.25) * mm});
            skLineSegment(sketch, "E91.MirrorCS", {"start": v(0, -74.25) * mm, "end": v(0, -104.25) * mm});
            skCircle(sketch, "E92.MirrorC", {"center": v(0, -104.25) * mm, "radius": 6 * mm});
            skLineSegment(sketch, "E93", {"start": v(0, 80) * mm, "end": v(0, 110) * mm});
            skSolve(sketch);
        }
        {
            var Q0;
            Q0=makeQuery(id+"F16.imprint","IMPRINT",FACE,{"disambiguationData":[TD([[makeQuery(id+"F16.imprint","IMPRINT",EDGE,{"derivedFrom":sQuery(id+"F16.wireOp",EDGE,"E80")}),-1.0]])]});
            var Q1;
            {var subQ7=sQuery(id+"F16.wireOp",EDGE,"E79.1");Q1=makeQuery(id+"F16.imprint","IMPRINT",FACE,{"disambiguationData":[TD([[makeQuery(id+"F16.imprint","IMPRINT",EDGE,{"derivedFrom":subQ7}),1.0]])]});}
            var Q2;
            {var subQ0=sQuery(id+"F16.wireOp",EDGE,"E86.MirrorCS");Q2=makeQuery(id+"F16.imprint","IMPRINT",FACE,{"disambiguationData":[TD([[makeQuery(id+"F16.imprint","IMPRINT",EDGE,{"derivedFrom":subQ0}),1.0]])]});}
            var Q3;
            Q3=makeQuery(id+"F2.opExtrude","CAP_FACE",FACE,{"disambiguationData":[OSD([sQuery(id+"F0.wireOp",EDGE,"E12"),sQuery(id+"F0.wireOp",EDGE,"E13"),sQuery(id+"F0.wireOp",EDGE,"E14"),sQuery(id+"F0.wireOp",EDGE,"E15"),sQuery(id+"F0.wireOp",EDGE,"E17.filletArc"),sQuery(id+"F0.wireOp",EDGE,"E18.filletArc"),sQuery(id+"F0.wireOp",EDGE,"E19.filletArc"),sQuery(id+"F0.wireOp",EDGE,"E20.filletArc"),sQuery(id+"F0.wireOp",EDGE,"E25.0"),sQuery(id+"F0.wireOp",EDGE,"E25.1"),sQuery(id+"F0.wireOp",EDGE,"E25.2"),sQuery(id+"F0.wireOp",EDGE,"E25.3"),sQuery(id+"F0.wireOp",EDGE,"E25.4"),sQuery(id+"F0.wireOp",EDGE,"E25.5"),sQuery(id+"F0.wireOp",EDGE,"E25.6"),sQuery(id+"F0.wireOp",EDGE,"E25.7")])],"isStart":false});
            extrude(context, id + "F17", {"entities" : qUnion([Q0, Q1, Q2]), "operationType" : NewBodyOperationType.ADD, "endBound" : BoundingType.UP_TO_SURFACE, "endBoundEntityFace" : qUnion([Q3]), "depth" : 25 * mm});
        }
    });
